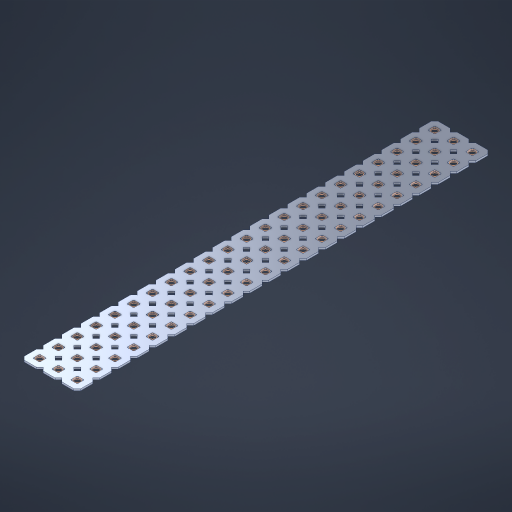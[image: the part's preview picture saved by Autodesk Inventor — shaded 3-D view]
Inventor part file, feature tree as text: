
AUTODESK INVENTOR PART (.ipt)
format: ipt  version: 2023 (Build 270158000, 158)  size: 1,025,024 bytes
history: native  units: in
note: dims shown in document units (in); Inventor stores cm internally (conversion verified against a paired STEP export)
features: other x67, extrude x65, sketch x2, pattern_linear x1
ambient origin geometry x8: Origin, YZ Plane, XZ Plane, XY Plane, X Axis, Y Axis, Z Axis, Center Point
bodies: Solid1 (feature_tree), Body (feature_tree)
feature tree (135):
  pattern_linear  "Rectangular Pattern1"  Spacing1=0.09in  [1 undecoded]
  sketch  "Sketch1"  dims[d1=0.5in]
  sketch  "Sketch2"  dims[d2=0.182in d3=0.09in d4=0.09in d5=0.09in d6=0.09in d7=0.09in d8=0.09in d9=0.09in d10=0.09in d11=0.02in d13=0.0in d14=0.172in d15=0.0625in d16=0.0in d19=0.5in d22=0.5in]
  other  "Srf1"
  other  "Srf126"
  other  "Srf127"
  other  "Srf128"
  other  "Srf129"
  other  "Srf130"
  other  "Srf131"
  other  "Srf250"
  other  "Srf251"
  other  "Srf252"
  other  "Srf253"
  other  "Srf254"
  other  "Srf255"
  other  "Srf256"
  other  "Srf257"
  other  "Srf258"
  other  "Srf259"
  other  "Srf260"
  other  "Srf261"
  other  "Srf262"
  other  "Srf263"
  other  "Srf264"
  other  "Srf268"
  other  "Srf269"
  other  "Srf270"
  other  "Srf271"
  other  "Srf272"
  other  "Srf273"
  other  "Srf274"
  other  "Srf275"
  other  "Srf276"
  other  "Srf277"
  other  "Srf278"
  other  "Srf279"
  other  "Srf280"
  other  "Srf281"
  other  "Srf282"
  other  "Srf283"
  other  "Srf284"
  other  "Srf285"
  other  "Srf286"
  other  "Srf287"
  other  "Srf288"
  other  "Srf289"
  other  "Srf293"
  other  "Srf294"
  other  "Srf295"
  other  "Srf296"
  other  "Srf297"
  other  "Srf298"
  other  "Srf299"
  other  "Srf300"
  other  "Srf301"
  other  "Srf302"
  other  "Srf303"
  other  "Srf304"
  other  "Srf305"
  other  "Srf306"
  other  "Srf307"
  other  "Srf308"
  other  "Srf309"
  other  "Srf310"
  other  "Srf311"
  other  "Srf312"
  other  "Srf313"
  other  "Srf314"
  other  "Circle"
  extrude  "ExtrusionSrf126"  Depth=0.09in
  extrude  "ExtrusionSrf127"  Depth=0.09in
  extrude  "ExtrusionSrf128"  Depth=0.09in
  extrude  "ExtrusionSrf129"  Depth=0.09in
  extrude  "ExtrusionSrf130"  Depth=0.09in
  extrude  "ExtrusionSrf131"  Depth=0.09in
  extrude  "ExtrusionSrf250"  Depth=0.09in
  extrude  "ExtrusionSrf251"  Depth=0.02in
  extrude  "ExtrusionSrf252"  TaperAngle=0.0deg  [1 undecoded]
  extrude  "ExtrusionSrf253"  Depth=0.5in
  extrude  "ExtrusionSrf254"  Depth=0.5in TaperAngle=0.0deg
  extrude  "ExtrusionSrf255"  Depth=0.5in
  extrude  "ExtrusionSrf256"  Depth=0.5in
  extrude  "ExtrusionSrf257"  [1 undecoded]
  extrude  "ExtrusionSrf258"  [1 undecoded]
  extrude  "ExtrusionSrf259"  [1 undecoded]
  extrude  "ExtrusionSrf260"  [1 undecoded]
  extrude  "ExtrusionSrf261"  [1 undecoded]
  extrude  "ExtrusionSrf262"  [1 undecoded]
  extrude  "ExtrusionSrf263"  [1 undecoded]
  extrude  "ExtrusionSrf264"  [1 undecoded]
  extrude  "ExtrusionSrf268"  [1 undecoded]
  extrude  "ExtrusionSrf269"  [1 undecoded]
  extrude  "ExtrusionSrf270"  [1 undecoded]
  extrude  "ExtrusionSrf271"  [1 undecoded]
  extrude  "ExtrusionSrf272"  [1 undecoded]
  extrude  "ExtrusionSrf273"  [1 undecoded]
  extrude  "ExtrusionSrf274"  [1 undecoded]
  extrude  "ExtrusionSrf275"  [1 undecoded]
  extrude  "ExtrusionSrf276"  [1 undecoded]
  extrude  "ExtrusionSrf277"  [1 undecoded]
  extrude  "ExtrusionSrf278"  [1 undecoded]
  extrude  "ExtrusionSrf279"  [1 undecoded]
  extrude  "ExtrusionSrf280"  [1 undecoded]
  extrude  "ExtrusionSrf281"  [1 undecoded]
  extrude  "ExtrusionSrf282"  [1 undecoded]
  extrude  "ExtrusionSrf283"  [1 undecoded]
  extrude  "ExtrusionSrf284"  [1 undecoded]
  extrude  "ExtrusionSrf285"  [1 undecoded]
  extrude  "ExtrusionSrf286"  [1 undecoded]
  extrude  "ExtrusionSrf287"  [1 undecoded]
  extrude  "ExtrusionSrf288"  [1 undecoded]
  extrude  "ExtrusionSrf289"  [1 undecoded]
  extrude  "ExtrusionSrf293"  [1 undecoded]
  extrude  "ExtrusionSrf294"  [1 undecoded]
  extrude  "ExtrusionSrf295"  [1 undecoded]
  extrude  "ExtrusionSrf296"  [1 undecoded]
  extrude  "ExtrusionSrf297"  [1 undecoded]
  extrude  "ExtrusionSrf298"  [1 undecoded]
  extrude  "ExtrusionSrf299"  [1 undecoded]
  extrude  "ExtrusionSrf300"  [1 undecoded]
  extrude  "ExtrusionSrf301"  [1 undecoded]
  extrude  "ExtrusionSrf302"  [1 undecoded]
  extrude  "ExtrusionSrf303"  [1 undecoded]
  extrude  "ExtrusionSrf304"  [1 undecoded]
  extrude  "ExtrusionSrf305"  [1 undecoded]
  extrude  "ExtrusionSrf306"  [1 undecoded]
  extrude  "ExtrusionSrf307"  [1 undecoded]
  extrude  "ExtrusionSrf308"  [1 undecoded]
  extrude  "ExtrusionSrf309"  [1 undecoded]
  extrude  "ExtrusionSrf310"  [1 undecoded]
  extrude  "ExtrusionSrf311"  [1 undecoded]
  extrude  "ExtrusionSrf312"  [1 undecoded]
  extrude  "ExtrusionSrf313"  [1 undecoded]
  extrude  "ExtrusionSrf314"  [1 undecoded]
note: 54 required parameter values undecoded (feature->parameter linkage not recoverable at this tier; creation-order binding heuristic only, values carry confidence <= 0.55)
